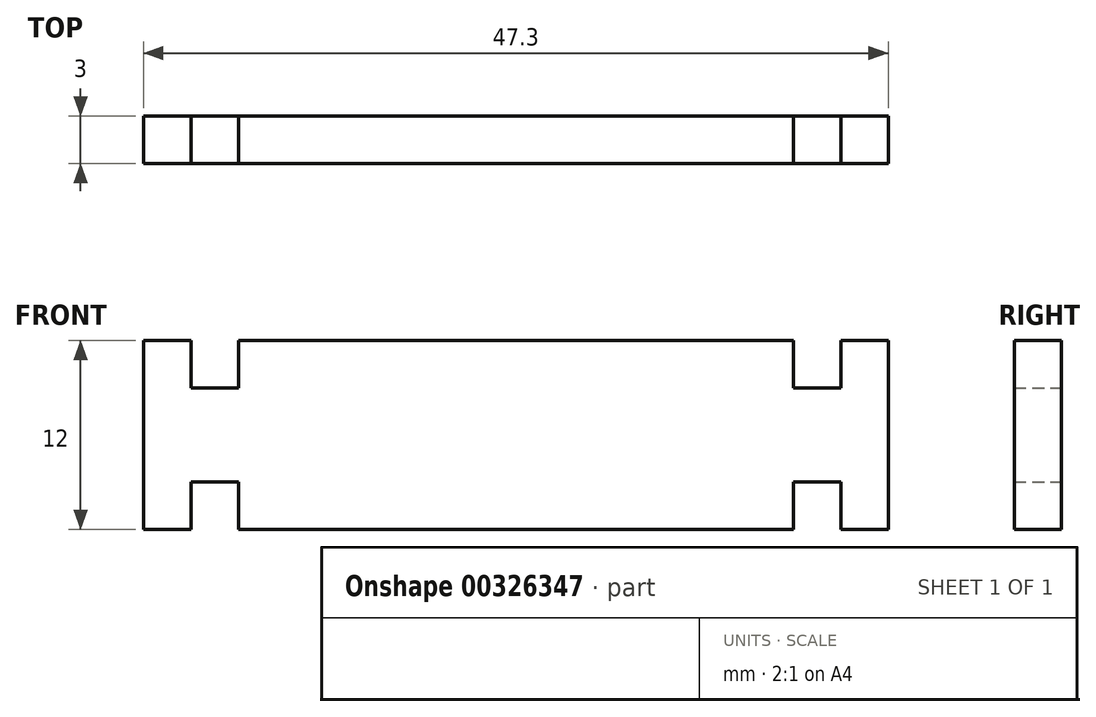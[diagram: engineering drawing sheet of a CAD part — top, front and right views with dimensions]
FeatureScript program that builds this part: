
annotation { "Feature Type Name" : "Feature", "Feature Type Description" : "" }
export const myFeature = defineFeature(function(context is Context, id is Id, definition is map)
    precondition{}
    {
        {
            var Q0;
            Q0=qCreatedBy(makeId("Front.planeOp"),FACE);
            var sketch = newSketch(context, id + "F0", { "sketchPlane" : qUnion([Q0])});
            skPoint(sketch, "E0", {"position": v(-22.15, 0) * mm});
            skPoint(sketch, "E1", {"position": v(-22.15, 3.02) * mm});
            skPoint(sketch, "E2", {"position": v(-19.11, 3.02) * mm});
            skPoint(sketch, "E3", {"position": v(19.15, 0) * mm});
            skPoint(sketch, "E4", {"position": v(19.15, 3.02) * mm});
            skPoint(sketch, "E5", {"position": v(16.1, 3.02) * mm});
            skPoint(sketch, "E6", {"position": v(16.1, 0) * mm});
            skLineSegment(sketch, "E7", {"start": v(-22.15, 0) * mm, "end": v(-22.15, 3.02) * mm});
            skLineSegment(sketch, "E8", {"start": v(-19.11, 3.02) * mm, "end": v(-22.15, 3.02) * mm});
            skLineSegment(sketch, "E9", {"start": v(-19.11, 0) * mm, "end": v(-19.11, 3.02) * mm});
            skLineSegment(sketch, "E10", {"start": v(16.1, 0) * mm, "end": v(16.1, 3.02) * mm});
            skLineSegment(sketch, "E11", {"start": v(19.15, 3.02) * mm, "end": v(16.1, 3.02) * mm});
            skLineSegment(sketch, "E12", {"start": v(19.15, 0) * mm, "end": v(19.15, 3.02) * mm});
            skLineSegment(sketch, "E13.trimOffspring", {"start": v(19.15, 0) * mm, "end": v(22.15, 0) * mm});
            skLineSegment(sketch, "E14.trimOffspring", {"start": v(-22.15, 0) * mm, "end": v(-25.15, 0) * mm});
            skLineSegment(sketch, "E15", {"start": v(-25.15, 12) * mm, "end": v(-22.15, 12) * mm});
            skLineSegment(sketch, "E16", {"start": v(-22.15, 12) * mm, "end": v(-22.15, 8.98) * mm});
            skLineSegment(sketch, "E17", {"start": v(-22.15, 8.98) * mm, "end": v(-19.11, 8.98) * mm});
            skLineSegment(sketch, "E18", {"start": v(-19.1, 8.98) * mm, "end": v(-19.1, 12) * mm});
            skLineSegment(sketch, "E19", {"start": v(22.15, 12) * mm, "end": v(19.15, 12) * mm});
            skLineSegment(sketch, "E20", {"start": v(19.15, 12) * mm, "end": v(19.15, 8.98) * mm});
            skLineSegment(sketch, "E21", {"start": v(19.15, 8.98) * mm, "end": v(16.1, 8.98) * mm});
            skLineSegment(sketch, "E22", {"start": v(16.1, 8.98) * mm, "end": v(16.1, 12) * mm});
            skLineSegment(sketch, "E23", {"start": v(16.1, 12) * mm, "end": v(-19.11, 12) * mm});
            skLineSegment(sketch, "E24", {"start": v(22.15, 12) * mm, "end": v(22.15, 0) * mm});
            skLineSegment(sketch, "E25", {"start": v(-25.15, 12) * mm, "end": v(-25.15, 0) * mm});
            skLineSegment(sketch, "E26", {"start": v(-19.11, 0) * mm, "end": v(16.1, 0) * mm});
            skSolve(sketch);
        }
        {
            var Q0;
            Q0=makeQuery(id+"F0.imprint","IMPRINT",FACE,{"disambiguationData":[TD([[makeQuery(id+"F0.imprint","IMPRINT",EDGE,{"derivedFrom":sQuery(id+"F0.wireOp",EDGE,"E7")}),1.0]])]});
            extrude(context, id + "F1", {"entities" : qUnion([Q0]), "depth" : 3 * mm});
        }
    });
